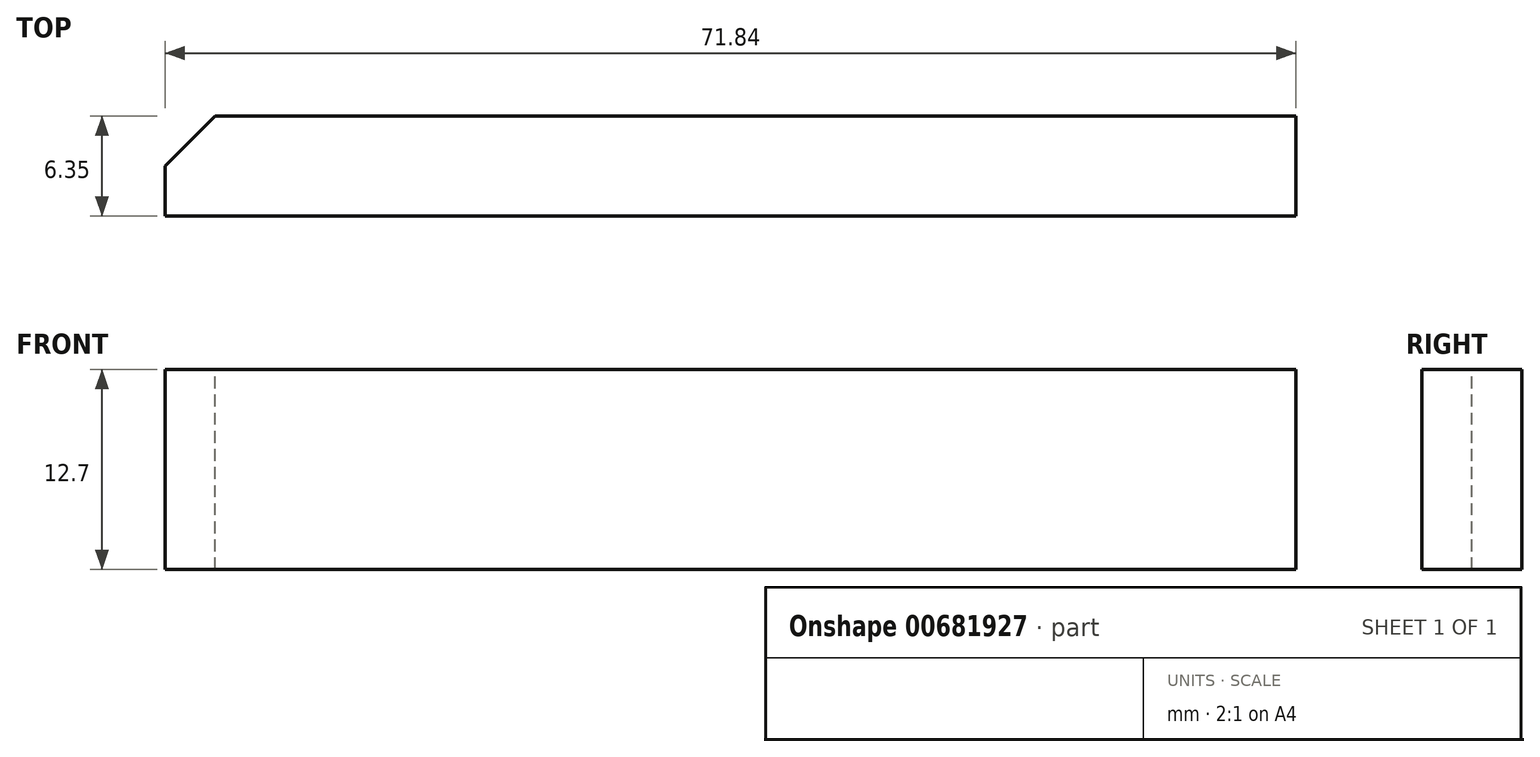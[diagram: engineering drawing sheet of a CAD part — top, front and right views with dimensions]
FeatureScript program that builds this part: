
annotation { "Feature Type Name" : "Feature", "Feature Type Description" : "" }
export const myFeature = defineFeature(function(context is Context, id is Id, definition is map)
    precondition{}
    {
        {
            var Q0;
            Q0=qCreatedBy(makeId("Right.planeOp"),FACE);
            var sketch = newSketch(context, id + "F0", { "sketchPlane" : qUnion([Q0])});
            skLineSegment(sketch, "E0.bottom", {"start": v(3.17, 6.35) * mm, "end": v(-3.18, 6.35) * mm});
            skLineSegment(sketch, "E0.top", {"start": v(3.17, -6.35) * mm, "end": v(-3.18, -6.35) * mm});
            skLineSegment(sketch, "E0.left", {"start": v(3.18, 6.35) * mm, "end": v(3.17, -6.35) * mm});
            skLineSegment(sketch, "E0.right", {"start": v(-3.18, 6.35) * mm, "end": v(-3.18, -6.35) * mm});
            skPoint(sketch, "E0.middle", {"position": v(0, 0) * mm});
            skSolve(sketch);
        }
        {
            var Q0;
            Q0 = qSketchRegion(id + "F0", true);
            extrude(context, id + "F1", {"entities" : qUnion([Q0]), "depth" : 71.84 * mm, "offsetDistance" : 25.4 * mm, "symmetric" : true});
        }
        {
            var Q0;
            Q0=qCreatedBy(makeId("Top.planeOp"),FACE);
            var sketch = newSketch(context, id + "F2", { "sketchPlane" : qUnion([Q0])});
            skLineSegment(sketch, "E1", {"start": v(-35.92, 0) * mm, "end": v(-32.75, 3.18) * mm});
            skLineSegment(sketch, "E2.0", {"start": v(-35.92, 3.17) * mm, "end": v(-35.92, 0) * mm});
            skLineSegment(sketch, "E3.0.1", {"start": v(-35.92, -3.18) * mm, "end": v(35.92, -3.18) * mm});
            skLineSegment(sketch, "E3.0.3", {"start": v(-32.75, 3.17) * mm, "end": v(-35.92, 3.17) * mm});
            skLineSegment(sketch, "E4.0.1", {"start": v(-35.92, -3.18) * mm, "end": v(35.92, -3.18) * mm, "construction": true});
            skLineSegment(sketch, "E5.0.2", {"start": v(35.92, -3.18) * mm, "end": v(35.92, 3.17) * mm, "construction": true});
            skSolve(sketch);
        }
        {
            var Q0;
            Q0 = qSketchRegion(id + "F2", true);
            extrude(context, id + "F3", {"entities" : qUnion([Q0]), "operationType" : NewBodyOperationType.REMOVE, "endBound" : BoundingType.THROUGH_ALL, "oppositeDirection" : true, "depth" : 25.4 * mm, "offsetDistance" : 25.4 * mm, "hasSecondDirection" : true, "secondDirectionBound" : BoundingType.THROUGH_ALL, "secondDirectionOppositeDirection" : false, "secondDirectionDepth" : 25.4 * mm});
        }
    });
